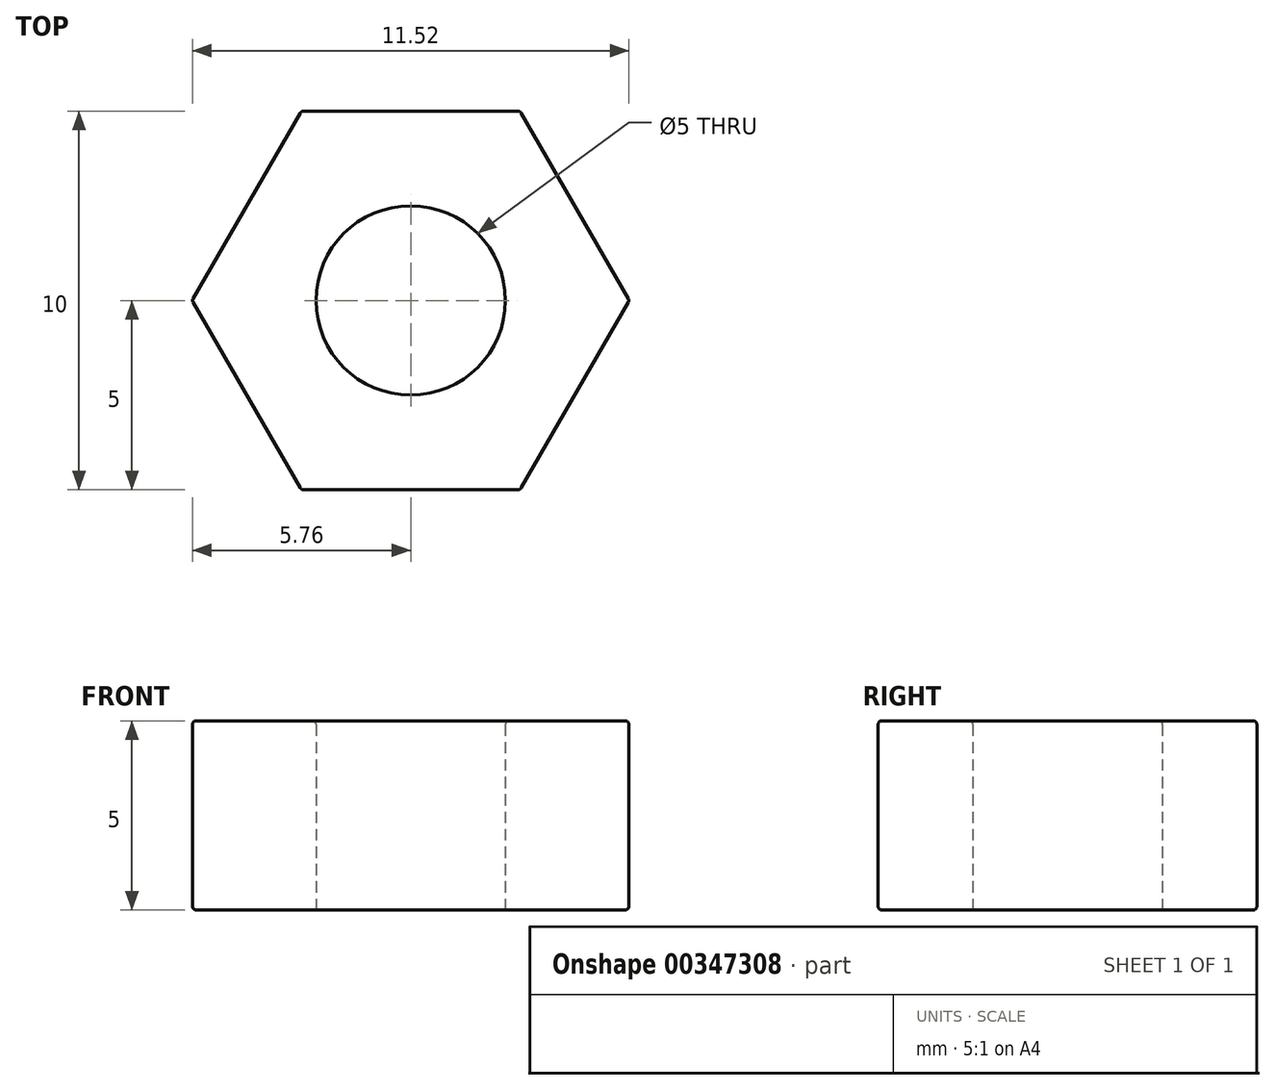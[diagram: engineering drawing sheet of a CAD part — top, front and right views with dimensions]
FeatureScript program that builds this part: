
annotation { "Feature Type Name" : "Feature", "Feature Type Description" : "" }
export const myFeature = defineFeature(function(context is Context, id is Id, definition is map)
    precondition{}
    {
        {
            var Q0;
            Q0=qCreatedBy(makeId("Top.planeOp"),FACE);
            var sketch = newSketch(context, id + "F0", { "sketchPlane" : qUnion([Q0])});
            skCircle(sketch, "E0.cCircle", {"center": v(0, 0) * mm, "radius": 5 * mm, "construction": true});
            skLineSegment(sketch, "E0.0", {"start": v(2.89, 5) * mm, "end": v(5.77, 0) * mm});
            skLineSegment(sketch, "E0.1", {"start": v(5.77, 0) * mm, "end": v(2.89, -5) * mm});
            skLineSegment(sketch, "E0.2", {"start": v(2.89, -5) * mm, "end": v(-2.89, -5) * mm});
            skLineSegment(sketch, "E0.3", {"start": v(-2.89, -5) * mm, "end": v(-5.77, 0) * mm});
            skLineSegment(sketch, "E0.4", {"start": v(-5.77, 0) * mm, "end": v(-2.89, 5) * mm});
            skLineSegment(sketch, "E0.5", {"start": v(-2.89, 5) * mm, "end": v(2.89, 5) * mm});
            skPoint(sketch, "E0.0.midPoint", {"position": v(4.33, 2.5) * mm});
            skCircle(sketch, "E1", {"center": v(0, 0) * mm, "radius": 2.5 * mm});
            skSolve(sketch);
        }
        {
            var Q0;
            Q0=makeQuery(id+"F0.imprint","IMPRINT",FACE,{"disambiguationData":[TD([[makeQuery(id+"F0.imprint","IMPRINT",EDGE,{"derivedFrom":sQuery(id+"F0.wireOp",EDGE,"E0.0")}),-1.0]])]});
            extrude(context, id + "F1", {"entities" : qUnion([Q0]), "depth" : 5 * mm});
        }
        {
            var Q0;
            Q0=makeQuery(id+"F1.opExtrude","SWEPT_FACE",FACE,{"disambiguationData":[OSD([sQuery(id+"F0.wireOp",EDGE,"E0.2")])]});
            var Q1;
            Q1=makeQuery(id+"F1.opExtrude","SWEPT_FACE",FACE,{"disambiguationData":[OSD([sQuery(id+"F0.wireOp",EDGE,"E0.3")])]});
            var Q2;
            Q2=makeQuery(id+"F1.opExtrude","SWEPT_FACE",FACE,{"disambiguationData":[OSD([sQuery(id+"F0.wireOp",EDGE,"E0.1")])]});
            var Q3;
            Q3=makeQuery(id+"F1.opExtrude","SWEPT_FACE",FACE,{"disambiguationData":[OSD([sQuery(id+"F0.wireOp",EDGE,"E0.0")])]});
            var Q4;
            Q4=makeQuery(id+"F1.opExtrude","SWEPT_FACE",FACE,{"disambiguationData":[OSD([sQuery(id+"F0.wireOp",EDGE,"E0.5")])]});
            var Q5;
            Q5=makeQuery(id+"F1.opExtrude","SWEPT_FACE",FACE,{"disambiguationData":[OSD([sQuery(id+"F0.wireOp",EDGE,"E0.4")])]});
            var Q6;
            Q6=makeQuery(id+"F1.opExtrude","CAP_EDGE",EDGE,{"disambiguationData":[OSD([sQuery(id+"F0.wireOp",EDGE,"E0.0")])],"isStart":true});
            var Q7;
            Q7=makeQuery(id+"F1.opExtrude","CAP_FACE",FACE,{"disambiguationData":[OSD([sQuery(id+"F0.wireOp",EDGE,"E0.0"),sQuery(id+"F0.wireOp",EDGE,"E0.1"),sQuery(id+"F0.wireOp",EDGE,"E0.2"),sQuery(id+"F0.wireOp",EDGE,"E0.3"),sQuery(id+"F0.wireOp",EDGE,"E0.4"),sQuery(id+"F0.wireOp",EDGE,"E0.5"),sQuery(id+"F0.wireOp",EDGE,"E1")])],"isStart":false});
            fillet(context, id + "F2", {"entities" : qUnion([Q0, Q1, Q2, Q3, Q4, Q5, Q6, Q7]), "radius" : 0.1 * mm, "tangentPropagation" : true, "allowEdgeOverflow" : false});
        }
    });
